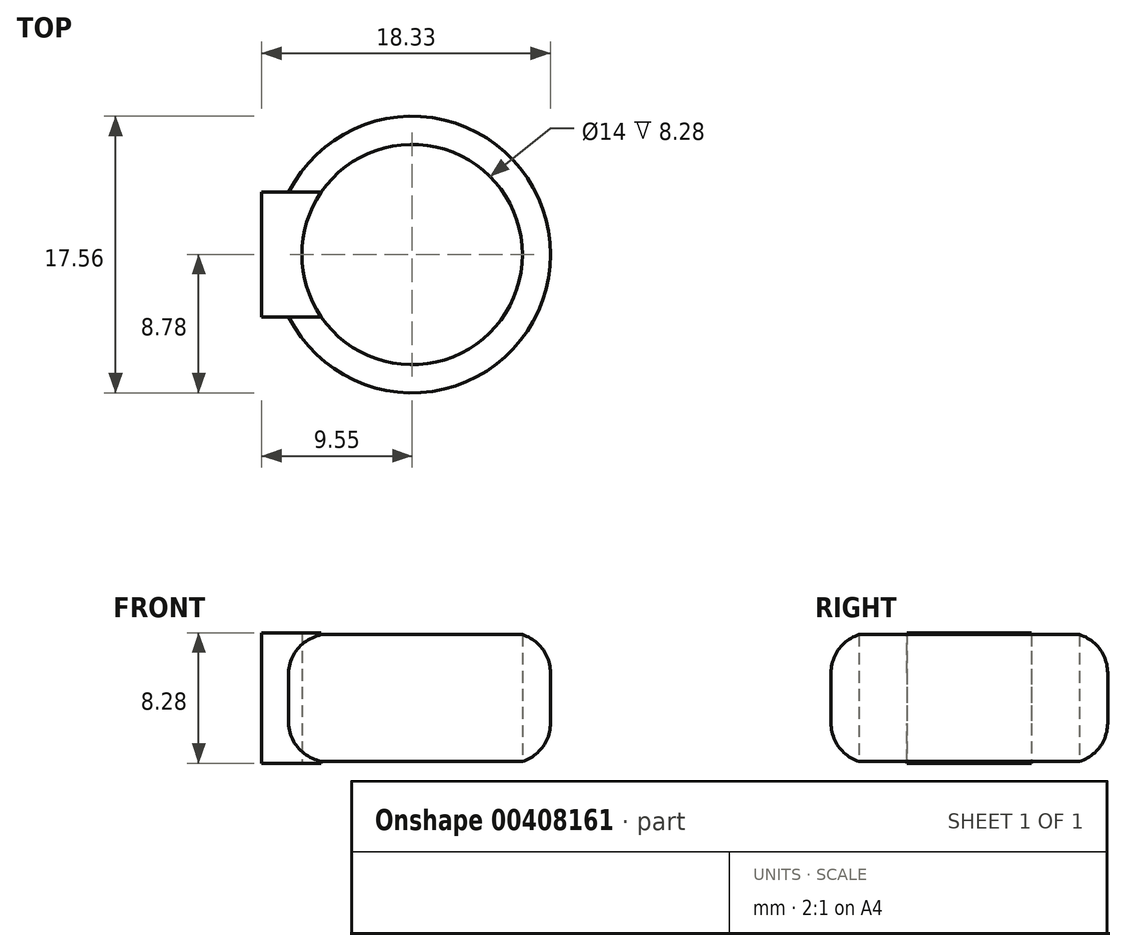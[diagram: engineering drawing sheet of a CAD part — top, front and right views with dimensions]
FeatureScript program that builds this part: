
annotation { "Feature Type Name" : "Feature", "Feature Type Description" : "" }
export const myFeature = defineFeature(function(context is Context, id is Id, definition is map)
    precondition{}
    {
        {
            var Q0;
            Q0=qCreatedBy(makeId("Top.planeOp"),FACE);
            var sketch = newSketch(context, id + "F0", { "sketchPlane" : qUnion([Q0])});
            skCircle(sketch, "E0", {"center": v(0, 0) * mm, "radius": 8.78 * mm});
            skCircle(sketch, "E1", {"center": v(0, 0) * mm, "radius": 7 * mm});
            skLineSegment(sketch, "E2.bottom", {"start": v(-9.55, -3.95) * mm, "end": v(-7.84, -3.95) * mm});
            skLineSegment(sketch, "E2.top", {"start": v(-9.55, 3.95) * mm, "end": v(-7.84, 3.95) * mm});
            skLineSegment(sketch, "E2.left", {"start": v(-9.55, -3.95) * mm, "end": v(-9.55, 3.95) * mm});
            skLineSegment(sketch, "E2.right", {"start": v(-7.84, -3.95) * mm, "end": v(-7.84, 3.95) * mm});
            skSolve(sketch);
        }
        {
            var Q0;
            Q0 = qSketchRegion(id + "F0", true);
            extrude(context, id + "F1", {"entities" : qUnion([Q0]), "depth" : 8.28 * mm});
        }
        {
            var Q0;
            Q0=makeQuery(id+"F1.opExtrude","CAP_EDGE",EDGE,{"disambiguationData":[OSD([sQuery(id+"F0.wireOp",EDGE,"E0")])],"isStart":false});
            fillet(context, id + "F2", {"entities" : qUnion([Q0]), "radius" : 2.54 * mm, "tangentPropagation" : true, "allowEdgeOverflow" : false});
        }
        {
            var Q0;
            Q0=makeQuery(id+"F1.opExtrude","CAP_EDGE",EDGE,{"disambiguationData":[OSD([sQuery(id+"F0.wireOp",EDGE,"E0")])],"isStart":true});
            fillet(context, id + "F3", {"entities" : qUnion([Q0]), "radius" : 2.54 * mm, "tangentPropagation" : true, "allowEdgeOverflow" : false});
        }
    });
